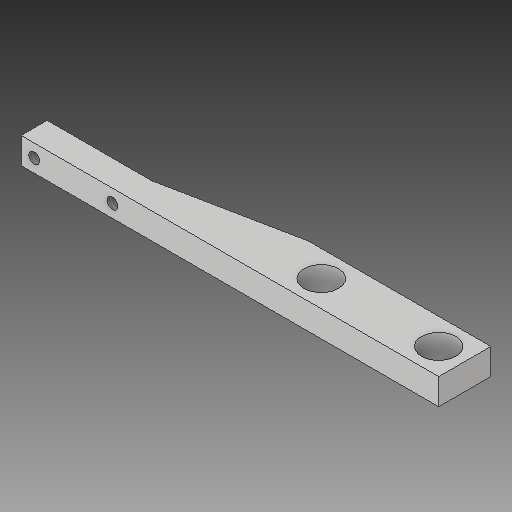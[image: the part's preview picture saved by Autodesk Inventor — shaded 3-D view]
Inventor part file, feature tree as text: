
AUTODESK INVENTOR PART (.ipt)
format: ipt  version: 2017 (Build 210142000, 142)  size: 102,912 bytes
history: native  units: in
note: dims shown in document units (in); Inventor stores cm internally (conversion verified against a paired STEP export)
features: other x3, sketch x3
ambient origin geometry x8: Origin, YZ Plane, XZ Plane, XY Plane, X Axis, Y Axis, Z Axis, Center Point
bodies: Solid1 (feature_tree)
feature tree (6):
  other  "WheelSuspensionFork.ipt"
  other  "Solid1::WheelSuspensionFork.ipt"
  other  "TaggingFeature1"
  sketch  "Sketch1"  dims[d0=0.3937in]
  sketch  "Sketch5"
  sketch  "Sketch6"
